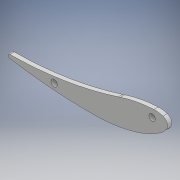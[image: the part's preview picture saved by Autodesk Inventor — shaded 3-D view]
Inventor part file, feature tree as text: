
AUTODESK INVENTOR PART (.ipt)
format: ipt  version: 2018.2 (Build 222227000, 227)  size: 122,880 bytes
history: native  units: mm
features: extrude x2, sketch x2, projected_geometry x1
ambient origin geometry x8: Origin, YZ Plane, XZ Plane, XY Plane, X Axis, Y Axis, Z Axis, Center Point
bodies: Body1 (feature_tree)
feature tree (5):
  extrude  "押し出し1"  Depth=4.0mm TaperAngle=0.0deg
  extrude  "押し出し2"  Depth=6.0mm
  sketch  "スケッチ1"
  projected_geometry  "投影ループ1"
  sketch  "スケッチ2"
